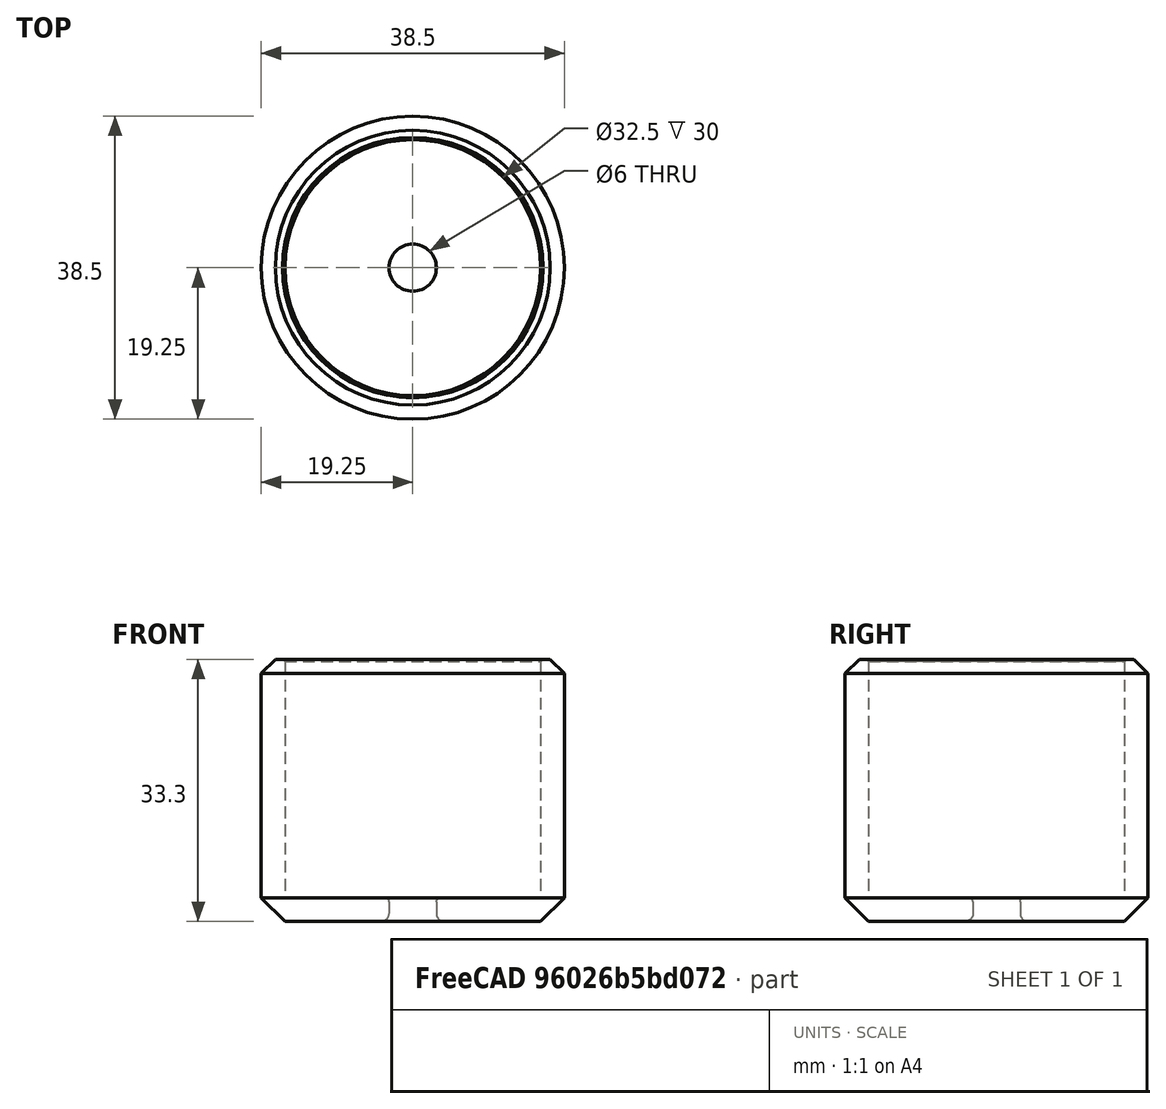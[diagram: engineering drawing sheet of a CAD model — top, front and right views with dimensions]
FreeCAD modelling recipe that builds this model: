
FCSTD DOCUMENT  (FreeCAD 1.1R44227 +568 (Git))
Label: bottom_plug
License: All rights reserved
LicenseURL: https://en.wikipedia.org/wiki/All_rights_reserved
objects: Sketcher::SketchObject×1, PartDesign::Revolution×1, PartDesign::Body×1, App::Point×1
note: 6 computed .brp shape members not serialized (recipe doc carries the construction recipe); baked Part::Feature solids carry a one-line shape summary decoded from their .brp

FEATURE [Sketcher::SketchObject] Sketch
  ArcFitTolerance = 1e-06
  AttachmentSupport = -> [XZ_Plane]
  ExternalTypes = [0]
  FullyConstrained = true
  MakeInternals = false
  MapMode = 5
  Placement = pos=(0,0,0) rot=(1,0,0;1.5708rad)
  _ExternalGeoVersion = 0
  sketch-geometry (20):
    g0: LineSegment StartX=-16.25 StartY=33 StartZ=0 EndX=-16.25 EndY=3 EndZ=0
    g1: LineSegment StartX=-16.25 StartY=3 StartZ=0 EndX=-3.5 EndY=3 EndZ=0
    g2: LineSegment StartX=-3 StartY=2.5 StartZ=0 EndX=-3 EndY=1 EndZ=0
    g3: LineSegment StartX=-4 StartY=0 StartZ=0 EndX=-16.25 EndY=0 EndZ=0
    g4: LineSegment StartX=-19.25 StartY=3 StartZ=0 EndX=-19.25 EndY=31.5 EndZ=0
    g5: LineSegment StartX=-17.45 StartY=33.3 StartZ=0 EndX=-16.55 EndY=33.3 EndZ=0
    g6: ArcOfCircle [constr] CenterX=-16.55 CenterY=33 CenterZ=0 NormalX=0 NormalY=0 NormalZ=1 AngleXU=0 Radius=0.3 StartAngle=-3.6e-15 EndAngle=1.5708
    g7: GeomPoint [constr] X=-16.25 Y=33.3 Z=0
    g8: LineSegment StartX=-16.25 StartY=33 StartZ=0 EndX=-16.55 EndY=33.3 EndZ=0
    g9: GeomPoint [constr] X=-19.25 Y=0 Z=0
    g10: ArcOfCircle CenterX=-4 CenterY=1 CenterZ=0 NormalX=0 NormalY=0 NormalZ=1 AngleXU=0 Radius=1 StartAngle=4.71239 EndAngle=6.28319
    g11: GeomPoint [constr] X=-3 Y=0 Z=0
    g12: ArcOfCircle CenterX=-3.5 CenterY=2.5 CenterZ=0 NormalX=0 NormalY=0 NormalZ=1 AngleXU=0 Radius=0.5 StartAngle=0 EndAngle=1.5708
    g13: GeomPoint [constr] X=-3 Y=3 Z=0
    g14: ArcOfCircle [constr] CenterX=-17.45 CenterY=31.5 CenterZ=0 NormalX=0 NormalY=0 NormalZ=1 AngleXU=0 Radius=1.8 StartAngle=1.5708 EndAngle=3.14159
    g15: GeomPoint [constr] X=-19.25 Y=33.3 Z=0
    g16: LineSegment StartX=-17.45 StartY=33.3 StartZ=0 EndX=-19.25 EndY=31.5 EndZ=0
    g17: ArcOfCircle [constr] CenterX=-16.25 CenterY=3 CenterZ=0 NormalX=0 NormalY=0 NormalZ=1 AngleXU=0 Radius=3 StartAngle=3.14159 EndAngle=4.71239
    g18: GeomPoint [constr] X=-19.25 Y=0 Z=0
    g19: LineSegment StartX=-19.25 StartY=3 StartZ=0 EndX=-16.25 EndY=0 EndZ=0
  constraints (45):
    c: Vertical(g0)
    c: Coincident(g1,g0)
    c: Horizontal(g1)
    c: Vertical(g2)
    c: Horizontal(g3)
    c: Vertical(g4)
    c: Horizontal(g5)
    c: PointOnObject(g7,g0)
    c: PointOnObject(g7,g5)
    c: Tangent(g0,g6) = 1.5708
    c: Tangent(g5,g6) = 1.5708
    c: Coincident(g8,g0)
    c: Coincident(g8,g5)
    c: PointOnObject(g11,g2)
    c: PointOnObject(g11,g3)
    c: Tangent(g2,g10) = 1.5708
    c: Tangent(g3,g10) = 1.5708
    c: PointOnObject(g13,g1)
    c: PointOnObject(g13,g2)
    c: Tangent(g1,g12) = 1.5708
    c: Tangent(g2,g12) = 1.5708
    c: DistanceX(g7,g-1) = 16.25
    c: DistanceX(g15,g7) = 3
    c: Radius(g6) = 0.3
    c: PointOnObject(g15,g4)
    c: PointOnObject(g15,g5)
    c: Tangent(g4,g14) = 1.5708
    c: Tangent(g5,g14) = 1.5708
    c: Coincident(g16,g4)
    c: Coincident(g16,g5)
    c: Radius(g14) = 1.8
    c: DistanceY(g11,g13) = 3
    c: Radius(g12) = 0.5
    c: Radius(g10) = 1
    c: DistanceX(g2,g-1) = 3
    c: PointOnObject(g3,g-1)
    c: DistanceY(g0,g0) = 30
    c: Coincident(g18,g9)
    c: PointOnObject(g18,g3)
    c: PointOnObject(g18,g4)
    c: Tangent(g3,g17) = 1.5708
    c: Tangent(g4,g17) = 1.5708
    c: Coincident(g19,g3)
    c: Coincident(g19,g4)
    c: Radius(g17) = 3
FEATURE [PartDesign::Revolution] Revolution
  Angle = 360
  Angle2 = 60
  Axis = (0,2e-16,1)
  Base = (0,0,0)
  FuseOrder = 1
  Placement = pos=(0,0,0) rot=(1,0,0;1.5708rad)
  Profile = -> Sketch
  ReferenceAxis = -> Sketch [V_Axis]
  Refine = true
  Suppressed = false
  Type = 0
FEATURE [PartDesign::Body] Body
  AllowCompound = false
  Group = -> [Sketch,Revolution]
  Origin = -> Origin
  Tip = -> Revolution
FEATURE [App::Point] Origin001  label="Origin"
  Role = Origin
